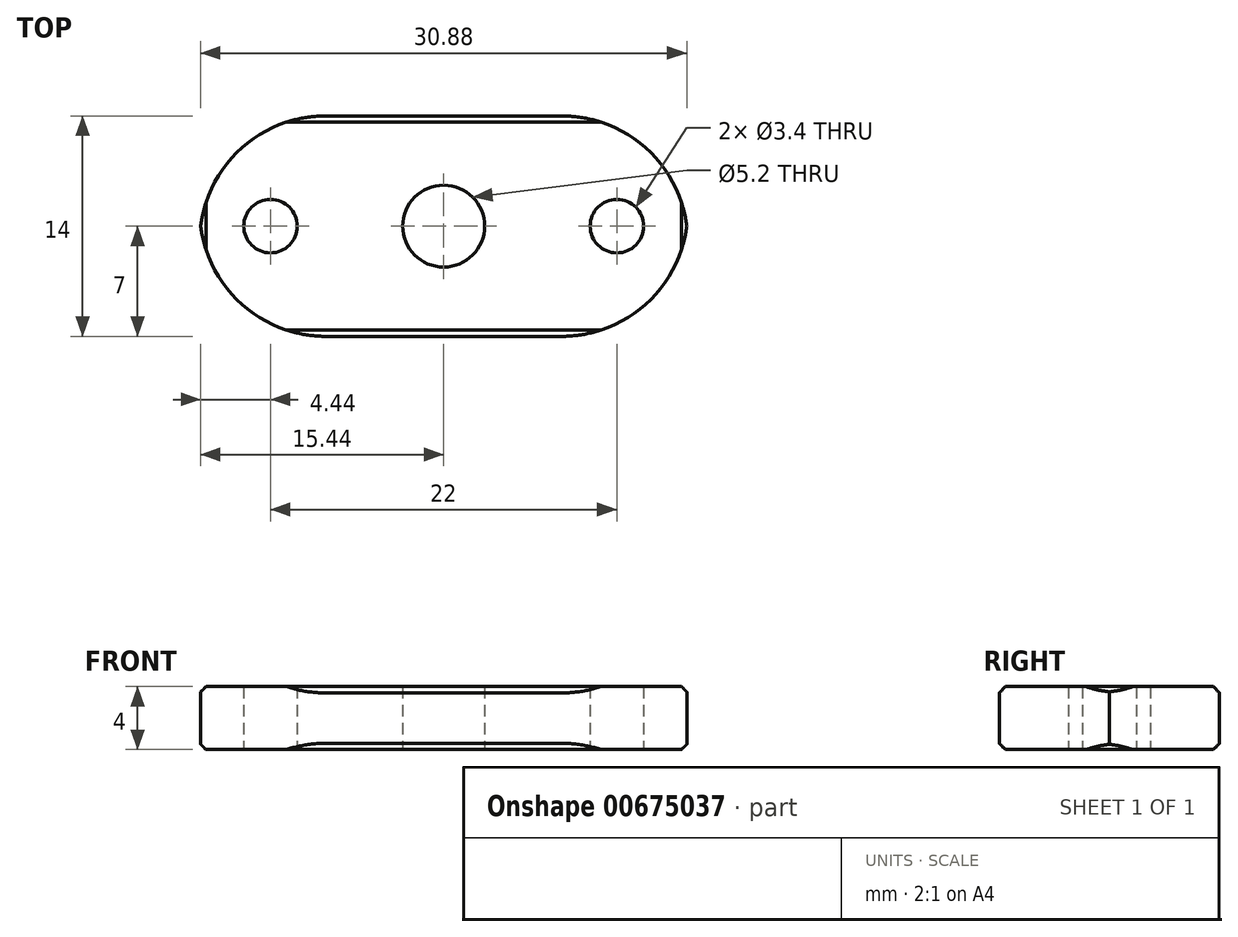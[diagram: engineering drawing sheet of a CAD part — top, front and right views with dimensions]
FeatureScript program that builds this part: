
annotation { "Feature Type Name" : "Feature", "Feature Type Description" : "" }
export const myFeature = defineFeature(function(context is Context, id is Id, definition is map)
    precondition{}
    {
        {
            var Q0;
            Q0=qCreatedBy(makeId("Top.planeOp"),FACE);
            var sketch = newSketch(context, id + "F0", { "sketchPlane" : qUnion([Q0])});
            skLineSegment(sketch, "E0.bottom", {"start": v(15.5, 7) * mm, "end": v(-15.5, 7) * mm});
            skLineSegment(sketch, "E0.top", {"start": v(15.5, -7) * mm, "end": v(-15.5, -7) * mm});
            skLineSegment(sketch, "E0.left", {"start": v(15.5, 7) * mm, "end": v(15.5, -7) * mm});
            skLineSegment(sketch, "E0.right", {"start": v(-15.5, 7) * mm, "end": v(-15.5, -7) * mm});
            skPoint(sketch, "E0.middle", {"position": v(0, 0) * mm});
            skCircle(sketch, "E1", {"center": v(0, 0) * mm, "radius": 2.6 * mm});
            skLineSegment(sketch, "E2", {"start": v(0, 0) * mm, "end": v(-11, 0) * mm});
            skCircle(sketch, "E3", {"center": v(-11, 0) * mm, "radius": 1.7 * mm});
            skCircle(sketch, "E4.MirrorC", {"center": v(11, 0) * mm, "radius": 1.7 * mm});
            skSolve(sketch);
        }
        {
            var Q0;
            Q0=makeQuery(id+"F0.imprint","IMPRINT",FACE,{"disambiguationData":[TD([[makeQuery(id+"F0.imprint","IMPRINT",EDGE,{"derivedFrom":sQuery(id+"F0.wireOp",EDGE,"E0.bottom")}),1.0]])]});
            extrude(context, id + "F1", {"entities" : qUnion([Q0]), "depth" : 4 * mm, "offsetDistance" : 25 * mm});
        }
        {
            var Q0;
            Q0=makeQuery(id+"F1.opExtrude","CAP_EDGE",EDGE,{"disambiguationData":[OSD([sQuery(id+"F0.wireOp",EDGE,"E0.top")])],"isStart":true});
            var Q1;
            Q1=makeQuery(id+"F1.opExtrude","CAP_EDGE",EDGE,{"disambiguationData":[OSD([sQuery(id+"F0.wireOp",EDGE,"E0.top")])],"isStart":false});
            var Q2;
            Q2=makeQuery(id+"F1.opExtrude","CAP_EDGE",EDGE,{"disambiguationData":[OSD([sQuery(id+"F0.wireOp",EDGE,"E0.left")])],"isStart":true});
            var Q3;
            Q3=makeQuery(id+"F1.opExtrude","CAP_EDGE",EDGE,{"disambiguationData":[OSD([sQuery(id+"F0.wireOp",EDGE,"E0.left")])],"isStart":false});
            var Q4;
            Q4=makeQuery(id+"F1.opExtrude","CAP_EDGE",EDGE,{"disambiguationData":[OSD([sQuery(id+"F0.wireOp",EDGE,"E0.bottom")])],"isStart":true});
            var Q5;
            Q5=makeQuery(id+"F1.opExtrude","CAP_EDGE",EDGE,{"disambiguationData":[OSD([sQuery(id+"F0.wireOp",EDGE,"E0.bottom")])],"isStart":false});
            var Q6;
            Q6=makeQuery(id+"F1.opExtrude","CAP_EDGE",EDGE,{"disambiguationData":[OSD([sQuery(id+"F0.wireOp",EDGE,"E0.right")])],"isStart":false});
            var Q7;
            Q7=makeQuery(id+"F1.opExtrude","CAP_EDGE",EDGE,{"disambiguationData":[OSD([sQuery(id+"F0.wireOp",EDGE,"E0.right")])],"isStart":true});
            chamfer(context, id + "F2", {"entities" : qUnion([Q0, Q1, Q2, Q3, Q4, Q5, Q6, Q7]), "width" : .4 * mm, "tangentPropagation" : true});
        }
        {
            var Q0;
            Q0=makeQuery(id+"F1.opExtrude","SWEPT_EDGE",EDGE,{"disambiguationData":[OSD([sQuery(id+"F0.wireOp",EDGE,"E0.bottom"),sQuery(id+"F0.wireOp",EDGE,"E0.right")])]});
            var Q1;
            Q1=makeQuery(id+"F1.opExtrude","SWEPT_EDGE",EDGE,{"disambiguationData":[OSD([sQuery(id+"F0.wireOp",EDGE,"E0.top"),sQuery(id+"F0.wireOp",EDGE,"E0.right")])]});
            var Q2;
            Q2=makeQuery(id+"F1.opExtrude","SWEPT_EDGE",EDGE,{"disambiguationData":[OSD([sQuery(id+"F0.wireOp",EDGE,"E0.bottom"),sQuery(id+"F0.wireOp",EDGE,"E0.left")])]});
            var Q3;
            Q3=makeQuery(id+"F1.opExtrude","SWEPT_EDGE",EDGE,{"disambiguationData":[OSD([sQuery(id+"F0.wireOp",EDGE,"E0.top"),sQuery(id+"F0.wireOp",EDGE,"E0.left")])]});
            fillet(context, id + "F3", {"entities" : qUnion([Q0, Q1, Q2, Q3]), "radius" : 8 * mm, "tangentPropagation" : true, "allowEdgeOverflow" : false});
        }
    });
